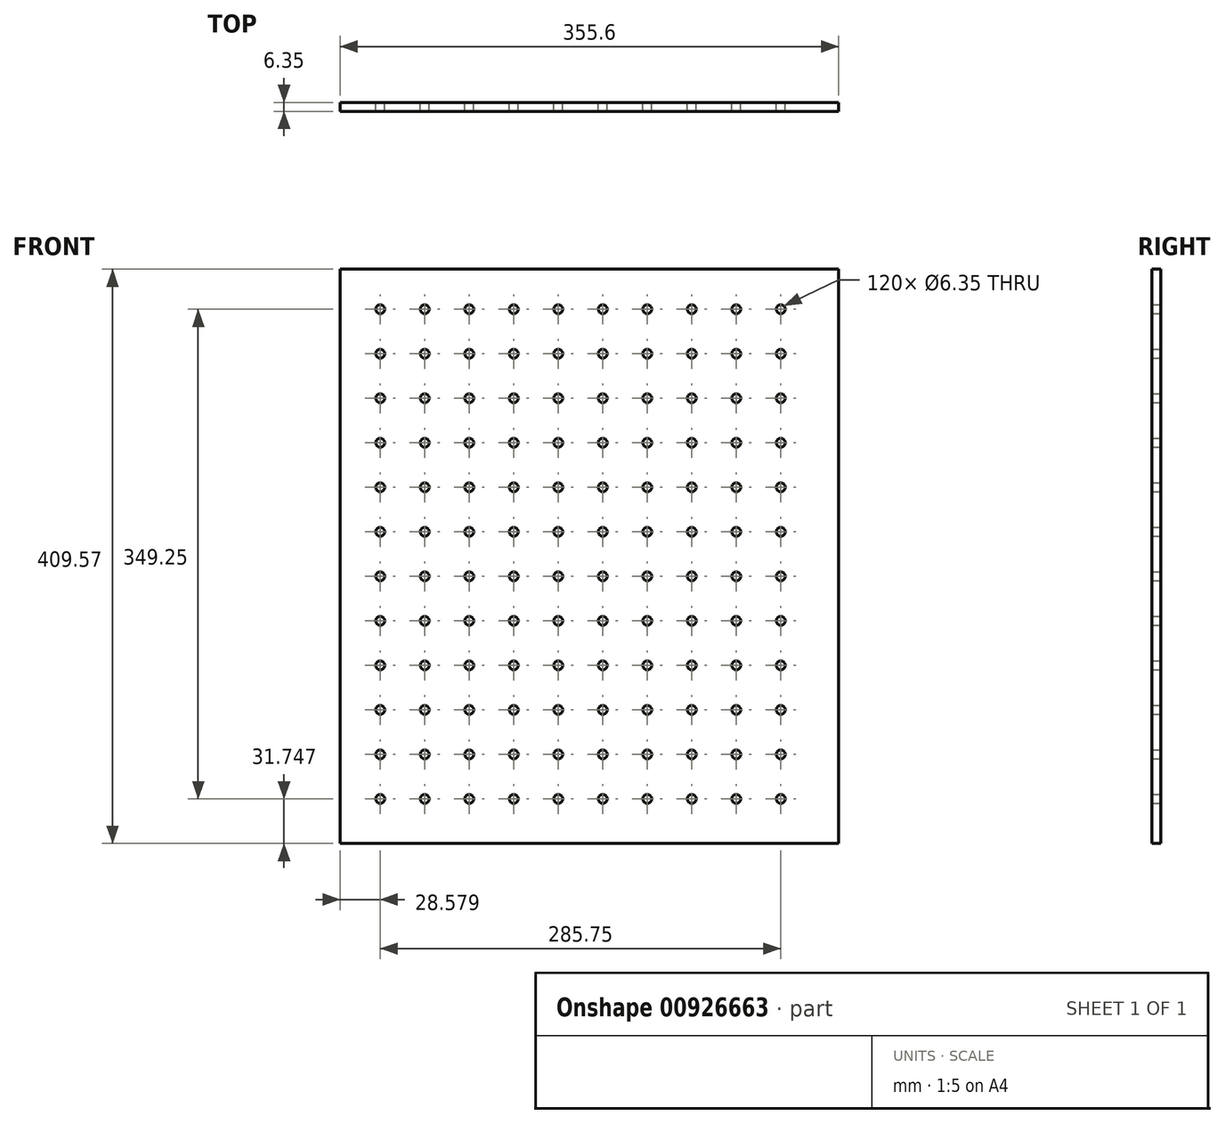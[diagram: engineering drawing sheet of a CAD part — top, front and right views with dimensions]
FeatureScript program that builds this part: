
annotation { "Feature Type Name" : "Feature", "Feature Type Description" : "" }
export const myFeature = defineFeature(function(context is Context, id is Id, definition is map)
    precondition{}
    {
        {
            var Q0;
            Q0=qCreatedBy(makeId("Front.planeOp"),FACE);
            var sketch = newSketch(context, id + "F0", { "sketchPlane" : qUnion([Q0])});
            skLineSegment(sketch, "E0.bottom", {"start": v(-178.08, 182.55) * mm, "end": v(177.52, 182.55) * mm});
            skLineSegment(sketch, "E0.top", {"start": v(-178.08, -227.02) * mm, "end": v(177.52, -227.02) * mm});
            skLineSegment(sketch, "E0.left", {"start": v(-178.08, 182.55) * mm, "end": v(-178.08, -227.02) * mm});
            skLineSegment(sketch, "E0.right", {"start": v(177.52, 182.55) * mm, "end": v(177.52, -227.02) * mm});
            skSolve(sketch);
        }
        {
            var Q0;
            Q0=makeQuery(id+"F0.imprint","IMPRINT",FACE,{"disambiguationData":[TD([[makeQuery(id+"F0.imprint","IMPRINT",EDGE,{"derivedFrom":sQuery(id+"F0.wireOp",EDGE,"E0.bottom")}),-1.0]])]});
            extrude(context, id + "F1", {"entities" : qUnion([Q0]), "depth" : 6.35 * mm, "offsetDistance" : 25.4 * mm});
        }
        {
            var Q0;
            Q0=makeQuery(id+"F1.opExtrude","CAP_FACE",FACE,{"disambiguationData":[OSD([sQuery(id+"F0.wireOp",EDGE,"E0.bottom"),sQuery(id+"F0.wireOp",EDGE,"E0.top"),sQuery(id+"F0.wireOp",EDGE,"E0.left"),sQuery(id+"F0.wireOp",EDGE,"E0.right")])],"isStart":false});
            var sketch = newSketch(context, id + "F2", { "sketchPlane" : qUnion([Q0])});
            skCircle(sketch, "E1", {"center": v(-149.5, 153.98) * mm, "radius": 3.18 * mm});
            skCircle(sketch, "E2", {"center": v(-117.75, 153.98) * mm, "radius": 3.18 * mm});
            skCircle(sketch, "E3", {"center": v(-86, 153.98) * mm, "radius": 3.18 * mm});
            skCircle(sketch, "E4", {"center": v(-54.25, 153.98) * mm, "radius": 3.18 * mm});
            skCircle(sketch, "E5", {"center": v(-22.5, 153.98) * mm, "radius": 3.18 * mm});
            skCircle(sketch, "E6", {"center": v(9.25, 153.98) * mm, "radius": 3.18 * mm});
            skCircle(sketch, "E7", {"center": v(41, 153.98) * mm, "radius": 3.18 * mm});
            skCircle(sketch, "E8", {"center": v(136.25, 153.98) * mm, "radius": 3.18 * mm});
            skCircle(sketch, "E9", {"center": v(104.5, 153.98) * mm, "radius": 3.18 * mm});
            skCircle(sketch, "E10", {"center": v(72.75, 153.98) * mm, "radius": 3.18 * mm});
            skSolve(sketch);
        }
        {
            var Q0;
            Q0=sQuery(id+"F2.wireOp",VERTEX,"E1.center");
            var Q1;
            Q1=sQuery(id+"F2.wireOp",VERTEX,"E2.center");
            var Q2;
            Q2=sQuery(id+"F2.wireOp",VERTEX,"E3.center");
            var Q3;
            Q3=sQuery(id+"F2.wireOp",VERTEX,"E4.center");
            var Q4;
            Q4=sQuery(id+"F2.wireOp",VERTEX,"E5.center");
            var Q5;
            Q5=sQuery(id+"F2.wireOp",VERTEX,"E6.center");
            var Q6;
            Q6=sQuery(id+"F2.wireOp",VERTEX,"E7.center");
            var Q7;
            Q7=sQuery(id+"F2.wireOp",VERTEX,"E10.center");
            var Q8;
            Q8=sQuery(id+"F2.wireOp",VERTEX,"E9.center");
            var Q9;
            Q9=sQuery(id+"F2.wireOp",VERTEX,"E8.center");
            var Q10;
            Q10=makeQuery(id+"F1.opExtrude","SWEPT_BODY",BODY,{"disambiguationData":[OSD([sQuery(id+"F0.wireOp",EDGE,"E0.bottom"),sQuery(id+"F0.wireOp",EDGE,"E0.top"),sQuery(id+"F0.wireOp",EDGE,"E0.left"),sQuery(id+"F0.wireOp",EDGE,"E0.right")])]});
            hole(context, id + "F3", {"style" : HoleStyle.SIMPLE, "endStyle" : HoleEndStyle.THROUGH, "holeDiameter" : 6.35 * mm, "majorDiameter" : 6.35 * mm, "isTappedThrough" : true, "tappedDepth" : 12.7 * mm, "tapClearance" : 3, "locations" : qUnion([Q0, Q1, Q2, Q3, Q4, Q5, Q6, Q7, Q8, Q9]), "scope" : qUnion([Q10])});
        }
        {
            var Q0;
            Q0=makeQuery(id+"F1.opExtrude","CAP_FACE",FACE,{"disambiguationData":[OSD([sQuery(id+"F0.wireOp",EDGE,"E0.bottom"),sQuery(id+"F0.wireOp",EDGE,"E0.top"),sQuery(id+"F0.wireOp",EDGE,"E0.left"),sQuery(id+"F0.wireOp",EDGE,"E0.right")])],"isStart":false});
            var sketch = newSketch(context, id + "F4", { "sketchPlane" : qUnion([Q0])});
            skCircle(sketch, "E11", {"center": v(-149.5, 122.23) * mm, "radius": 3.18 * mm});
            skCircle(sketch, "E12", {"center": v(-117.75, 122.23) * mm, "radius": 3.18 * mm});
            skCircle(sketch, "E13", {"center": v(-86, 122.23) * mm, "radius": 3.18 * mm});
            skCircle(sketch, "E14", {"center": v(-54.25, 122.23) * mm, "radius": 3.18 * mm});
            skCircle(sketch, "E15", {"center": v(-22.5, 122.23) * mm, "radius": 3.18 * mm});
            skCircle(sketch, "E16", {"center": v(9.25, 122.23) * mm, "radius": 3.18 * mm});
            skCircle(sketch, "E17", {"center": v(41, 122.23) * mm, "radius": 3.18 * mm});
            skCircle(sketch, "E18", {"center": v(136.25, 122.23) * mm, "radius": 3.18 * mm});
            skCircle(sketch, "E19", {"center": v(104.5, 122.23) * mm, "radius": 3.18 * mm});
            skCircle(sketch, "E20", {"center": v(72.75, 122.23) * mm, "radius": 3.18 * mm});
            skSolve(sketch);
        }
        {
            var Q0;
            Q0=sQuery(id+"F4.wireOp",VERTEX,"E11.center");
            var Q1;
            Q1=sQuery(id+"F4.wireOp",VERTEX,"E12.center");
            var Q2;
            Q2=sQuery(id+"F4.wireOp",VERTEX,"E13.center");
            var Q3;
            Q3=sQuery(id+"F4.wireOp",VERTEX,"E14.center");
            var Q4;
            Q4=sQuery(id+"F4.wireOp",VERTEX,"E15.center");
            var Q5;
            Q5=sQuery(id+"F4.wireOp",VERTEX,"E16.center");
            var Q6;
            Q6=sQuery(id+"F4.wireOp",VERTEX,"E17.center");
            var Q7;
            Q7=sQuery(id+"F4.wireOp",VERTEX,"E20.center");
            var Q8;
            Q8=sQuery(id+"F4.wireOp",VERTEX,"E19.center");
            var Q9;
            Q9=sQuery(id+"F4.wireOp",VERTEX,"E18.center");
            var Q10;
            Q10=makeQuery(id+"F1.opExtrude","SWEPT_BODY",BODY,{"disambiguationData":[OSD([sQuery(id+"F0.wireOp",EDGE,"E0.bottom"),sQuery(id+"F0.wireOp",EDGE,"E0.top"),sQuery(id+"F0.wireOp",EDGE,"E0.left"),sQuery(id+"F0.wireOp",EDGE,"E0.right")])]});
            hole(context, id + "F5", {"style" : HoleStyle.SIMPLE, "endStyle" : HoleEndStyle.THROUGH, "holeDiameter" : 6.35 * mm, "majorDiameter" : 6.35 * mm, "isTappedThrough" : true, "tappedDepth" : 12.7 * mm, "tapClearance" : 3, "locations" : qUnion([Q0, Q1, Q2, Q3, Q4, Q5, Q6, Q7, Q8, Q9]), "scope" : qUnion([Q10])});
        }
        {
            var Q0;
            Q0=makeQuery(id+"F1.opExtrude","CAP_FACE",FACE,{"disambiguationData":[OSD([sQuery(id+"F0.wireOp",EDGE,"E0.bottom"),sQuery(id+"F0.wireOp",EDGE,"E0.top"),sQuery(id+"F0.wireOp",EDGE,"E0.left"),sQuery(id+"F0.wireOp",EDGE,"E0.right")])],"isStart":false});
            var sketch = newSketch(context, id + "F6", { "sketchPlane" : qUnion([Q0])});
            skCircle(sketch, "E21", {"center": v(-149.5, 90.48) * mm, "radius": 3.18 * mm});
            skCircle(sketch, "E22", {"center": v(-117.75, 90.48) * mm, "radius": 3.18 * mm});
            skCircle(sketch, "E23", {"center": v(-86, 90.48) * mm, "radius": 3.18 * mm});
            skCircle(sketch, "E24", {"center": v(-54.25, 90.48) * mm, "radius": 3.18 * mm});
            skCircle(sketch, "E25", {"center": v(-22.5, 90.48) * mm, "radius": 3.18 * mm});
            skCircle(sketch, "E26", {"center": v(9.25, 90.48) * mm, "radius": 3.18 * mm});
            skCircle(sketch, "E27", {"center": v(41, 90.48) * mm, "radius": 3.18 * mm});
            skCircle(sketch, "E28", {"center": v(136.25, 90.48) * mm, "radius": 3.18 * mm});
            skCircle(sketch, "E29", {"center": v(104.5, 90.48) * mm, "radius": 3.18 * mm});
            skCircle(sketch, "E30", {"center": v(72.75, 90.48) * mm, "radius": 3.18 * mm});
            skCircle(sketch, "E31", {"center": v(-149.5, 58.73) * mm, "radius": 3.18 * mm});
            skCircle(sketch, "E32", {"center": v(-117.75, 58.73) * mm, "radius": 3.18 * mm});
            skCircle(sketch, "E33", {"center": v(-86, 58.73) * mm, "radius": 3.18 * mm});
            skCircle(sketch, "E34", {"center": v(-54.25, 58.73) * mm, "radius": 3.18 * mm});
            skCircle(sketch, "E35", {"center": v(-22.5, 58.73) * mm, "radius": 3.18 * mm});
            skCircle(sketch, "E36", {"center": v(9.25, 58.73) * mm, "radius": 3.18 * mm});
            skCircle(sketch, "E37", {"center": v(41, 58.73) * mm, "radius": 3.18 * mm});
            skCircle(sketch, "E38", {"center": v(136.25, 58.73) * mm, "radius": 3.18 * mm});
            skCircle(sketch, "E39", {"center": v(104.5, 58.73) * mm, "radius": 3.18 * mm});
            skCircle(sketch, "E40", {"center": v(72.75, 58.73) * mm, "radius": 3.18 * mm});
            skCircle(sketch, "E41", {"center": v(-149.5, 26.98) * mm, "radius": 3.18 * mm});
            skCircle(sketch, "E42", {"center": v(-117.75, 26.98) * mm, "radius": 3.18 * mm});
            skCircle(sketch, "E43", {"center": v(-86, 26.98) * mm, "radius": 3.18 * mm});
            skCircle(sketch, "E44", {"center": v(-54.25, 26.98) * mm, "radius": 3.18 * mm});
            skCircle(sketch, "E45", {"center": v(-22.5, 26.98) * mm, "radius": 3.18 * mm});
            skCircle(sketch, "E46", {"center": v(9.25, 26.98) * mm, "radius": 3.18 * mm});
            skCircle(sketch, "E47", {"center": v(41, 26.98) * mm, "radius": 3.18 * mm});
            skCircle(sketch, "E48", {"center": v(136.25, 26.98) * mm, "radius": 3.18 * mm});
            skCircle(sketch, "E49", {"center": v(104.5, 26.98) * mm, "radius": 3.18 * mm});
            skCircle(sketch, "E50", {"center": v(72.75, 26.98) * mm, "radius": 3.18 * mm});
            skCircle(sketch, "E51", {"center": v(-149.5, -4.77) * mm, "radius": 3.18 * mm});
            skCircle(sketch, "E52", {"center": v(-117.75, -4.77) * mm, "radius": 3.18 * mm});
            skCircle(sketch, "E53", {"center": v(-86, -4.77) * mm, "radius": 3.18 * mm});
            skCircle(sketch, "E54", {"center": v(-54.25, -4.77) * mm, "radius": 3.18 * mm});
            skCircle(sketch, "E55", {"center": v(-22.5, -4.77) * mm, "radius": 3.18 * mm});
            skCircle(sketch, "E56", {"center": v(9.25, -4.77) * mm, "radius": 3.18 * mm});
            skCircle(sketch, "E57", {"center": v(41, -4.77) * mm, "radius": 3.18 * mm});
            skCircle(sketch, "E58", {"center": v(136.25, -4.77) * mm, "radius": 3.18 * mm});
            skCircle(sketch, "E59", {"center": v(104.5, -4.77) * mm, "radius": 3.18 * mm});
            skCircle(sketch, "E60", {"center": v(72.75, -4.77) * mm, "radius": 3.18 * mm});
            skCircle(sketch, "E61", {"center": v(-149.5, -36.52) * mm, "radius": 3.18 * mm});
            skCircle(sketch, "E62", {"center": v(-117.75, -36.52) * mm, "radius": 3.18 * mm});
            skCircle(sketch, "E63", {"center": v(-86, -36.52) * mm, "radius": 3.18 * mm});
            skCircle(sketch, "E64", {"center": v(-54.25, -36.52) * mm, "radius": 3.18 * mm});
            skCircle(sketch, "E65", {"center": v(-22.5, -36.52) * mm, "radius": 3.18 * mm});
            skCircle(sketch, "E66", {"center": v(9.25, -36.52) * mm, "radius": 3.18 * mm});
            skCircle(sketch, "E67", {"center": v(41, -36.52) * mm, "radius": 3.18 * mm});
            skCircle(sketch, "E68", {"center": v(136.25, -36.52) * mm, "radius": 3.18 * mm});
            skCircle(sketch, "E69", {"center": v(104.5, -36.52) * mm, "radius": 3.18 * mm});
            skCircle(sketch, "E70", {"center": v(72.75, -36.52) * mm, "radius": 3.18 * mm});
            skCircle(sketch, "E71", {"center": v(-149.5, -68.27) * mm, "radius": 3.18 * mm});
            skCircle(sketch, "E72", {"center": v(-117.75, -68.27) * mm, "radius": 3.18 * mm});
            skCircle(sketch, "E73", {"center": v(-86, -68.27) * mm, "radius": 3.18 * mm});
            skCircle(sketch, "E74", {"center": v(-54.25, -68.27) * mm, "radius": 3.18 * mm});
            skCircle(sketch, "E75", {"center": v(-22.5, -68.27) * mm, "radius": 3.18 * mm});
            skCircle(sketch, "E76", {"center": v(9.25, -68.27) * mm, "radius": 3.18 * mm});
            skCircle(sketch, "E77", {"center": v(41, -68.27) * mm, "radius": 3.18 * mm});
            skCircle(sketch, "E78", {"center": v(136.25, -68.27) * mm, "radius": 3.18 * mm});
            skCircle(sketch, "E79", {"center": v(104.5, -68.27) * mm, "radius": 3.18 * mm});
            skCircle(sketch, "E80", {"center": v(72.75, -68.27) * mm, "radius": 3.18 * mm});
            skCircle(sketch, "E81", {"center": v(-149.5, -100.02) * mm, "radius": 3.18 * mm});
            skCircle(sketch, "E82", {"center": v(-117.75, -100.02) * mm, "radius": 3.18 * mm});
            skCircle(sketch, "E83", {"center": v(-86, -100.02) * mm, "radius": 3.18 * mm});
            skCircle(sketch, "E84", {"center": v(-54.25, -100.02) * mm, "radius": 3.18 * mm});
            skCircle(sketch, "E85", {"center": v(-22.5, -100.02) * mm, "radius": 3.18 * mm});
            skCircle(sketch, "E86", {"center": v(9.25, -100.02) * mm, "radius": 3.18 * mm});
            skCircle(sketch, "E87", {"center": v(41, -100.02) * mm, "radius": 3.18 * mm});
            skCircle(sketch, "E88", {"center": v(136.25, -100.02) * mm, "radius": 3.18 * mm});
            skCircle(sketch, "E89", {"center": v(104.5, -100.02) * mm, "radius": 3.18 * mm});
            skCircle(sketch, "E90", {"center": v(72.75, -100.02) * mm, "radius": 3.18 * mm});
            skCircle(sketch, "E91", {"center": v(-149.5, -131.77) * mm, "radius": 3.18 * mm});
            skCircle(sketch, "E92", {"center": v(-117.75, -131.77) * mm, "radius": 3.18 * mm});
            skCircle(sketch, "E93", {"center": v(-86, -131.77) * mm, "radius": 3.18 * mm});
            skCircle(sketch, "E94", {"center": v(-54.25, -131.77) * mm, "radius": 3.18 * mm});
            skCircle(sketch, "E95", {"center": v(-22.5, -131.77) * mm, "radius": 3.18 * mm});
            skCircle(sketch, "E96", {"center": v(9.25, -131.77) * mm, "radius": 3.18 * mm});
            skCircle(sketch, "E97", {"center": v(41, -131.77) * mm, "radius": 3.18 * mm});
            skCircle(sketch, "E98", {"center": v(136.25, -131.77) * mm, "radius": 3.18 * mm});
            skCircle(sketch, "E99", {"center": v(104.5, -131.77) * mm, "radius": 3.18 * mm});
            skCircle(sketch, "E100", {"center": v(72.75, -131.77) * mm, "radius": 3.18 * mm});
            skCircle(sketch, "E101", {"center": v(-149.5, -163.52) * mm, "radius": 3.18 * mm});
            skCircle(sketch, "E102", {"center": v(-117.75, -163.52) * mm, "radius": 3.18 * mm});
            skCircle(sketch, "E103", {"center": v(-86, -163.52) * mm, "radius": 3.18 * mm});
            skCircle(sketch, "E104", {"center": v(-54.25, -163.52) * mm, "radius": 3.18 * mm});
            skCircle(sketch, "E105", {"center": v(-22.5, -163.52) * mm, "radius": 3.18 * mm});
            skCircle(sketch, "E106", {"center": v(9.25, -163.52) * mm, "radius": 3.18 * mm});
            skCircle(sketch, "E107", {"center": v(41, -163.52) * mm, "radius": 3.18 * mm});
            skCircle(sketch, "E108", {"center": v(136.25, -163.52) * mm, "radius": 3.18 * mm});
            skCircle(sketch, "E109", {"center": v(104.5, -163.52) * mm, "radius": 3.18 * mm});
            skCircle(sketch, "E110", {"center": v(72.75, -163.52) * mm, "radius": 3.18 * mm});
            skCircle(sketch, "E111", {"center": v(-149.5, -195.27) * mm, "radius": 3.18 * mm});
            skCircle(sketch, "E112", {"center": v(-117.75, -195.27) * mm, "radius": 3.18 * mm});
            skCircle(sketch, "E113", {"center": v(-86, -195.27) * mm, "radius": 3.18 * mm});
            skCircle(sketch, "E114", {"center": v(-54.25, -195.27) * mm, "radius": 3.18 * mm});
            skCircle(sketch, "E115", {"center": v(-22.5, -195.27) * mm, "radius": 3.18 * mm});
            skCircle(sketch, "E116", {"center": v(9.25, -195.27) * mm, "radius": 3.18 * mm});
            skCircle(sketch, "E117", {"center": v(41, -195.27) * mm, "radius": 3.18 * mm});
            skCircle(sketch, "E118", {"center": v(136.25, -195.27) * mm, "radius": 3.18 * mm});
            skCircle(sketch, "E119", {"center": v(104.5, -195.27) * mm, "radius": 3.18 * mm});
            skCircle(sketch, "E120", {"center": v(72.75, -195.27) * mm, "radius": 3.18 * mm});
            skSolve(sketch);
        }
        {
            var Q0;
            Q0=sQuery(id+"F6.wireOp",VERTEX,"E60.center");
            var Q1;
            Q1=sQuery(id+"F6.wireOp",VERTEX,"E71.center");
            var Q2;
            Q2=sQuery(id+"F6.wireOp",VERTEX,"E30.center");
            var Q3;
            Q3=sQuery(id+"F6.wireOp",VERTEX,"E26.center");
            var Q4;
            Q4=sQuery(id+"F6.wireOp",VERTEX,"E105.center");
            var Q5;
            Q5=sQuery(id+"F6.wireOp",VERTEX,"E96.center");
            var Q6;
            Q6=sQuery(id+"F6.wireOp",VERTEX,"E31.center");
            var Q7;
            Q7=sQuery(id+"F6.wireOp",VERTEX,"E38.center");
            var Q8;
            Q8=sQuery(id+"F6.wireOp",VERTEX,"E98.center");
            var Q9;
            Q9=sQuery(id+"F6.wireOp",VERTEX,"E77.center");
            var Q10;
            Q10=sQuery(id+"F6.wireOp",VERTEX,"E101.center");
            var Q11;
            Q11=sQuery(id+"F6.wireOp",VERTEX,"E34.center");
            var Q12;
            Q12=sQuery(id+"F6.wireOp",VERTEX,"E52.center");
            var Q13;
            Q13=sQuery(id+"F6.wireOp",VERTEX,"E118.center");
            var Q14;
            Q14=sQuery(id+"F6.wireOp",VERTEX,"E115.center");
            var Q15;
            Q15=sQuery(id+"F6.wireOp",VERTEX,"E48.center");
            var Q16;
            Q16=sQuery(id+"F6.wireOp",VERTEX,"E111.center");
            var Q17;
            Q17=sQuery(id+"F6.wireOp",VERTEX,"E35.center");
            var Q18;
            Q18=sQuery(id+"F6.wireOp",VERTEX,"E44.center");
            var Q19;
            Q19=sQuery(id+"F6.wireOp",VERTEX,"E28.center");
            var Q20;
            Q20=sQuery(id+"F6.wireOp",VERTEX,"E21.center");
            var Q21;
            Q21=sQuery(id+"F6.wireOp",VERTEX,"E104.center");
            var Q22;
            Q22=sQuery(id+"F6.wireOp",VERTEX,"E86.center");
            var Q23;
            Q23=sQuery(id+"F6.wireOp",VERTEX,"E23.center");
            var Q24;
            Q24=sQuery(id+"F6.wireOp",VERTEX,"E64.center");
            var Q25;
            Q25=sQuery(id+"F6.wireOp",VERTEX,"E55.center");
            var Q26;
            Q26=sQuery(id+"F6.wireOp",VERTEX,"E87.center");
            var Q27;
            Q27=sQuery(id+"F6.wireOp",VERTEX,"E47.center");
            var Q28;
            Q28=sQuery(id+"F6.wireOp",VERTEX,"E84.center");
            var Q29;
            Q29=sQuery(id+"F6.wireOp",VERTEX,"E114.center");
            var Q30;
            Q30=sQuery(id+"F6.wireOp",VERTEX,"E72.center");
            var Q31;
            Q31=sQuery(id+"F6.wireOp",VERTEX,"E109.center");
            var Q32;
            Q32=sQuery(id+"F6.wireOp",VERTEX,"E65.center");
            var Q33;
            Q33=sQuery(id+"F6.wireOp",VERTEX,"E93.center");
            var Q34;
            Q34=sQuery(id+"F6.wireOp",VERTEX,"E116.center");
            var Q35;
            Q35=sQuery(id+"F6.wireOp",VERTEX,"E56.center");
            var Q36;
            Q36=sQuery(id+"F6.wireOp",VERTEX,"E81.center");
            var Q37;
            Q37=sQuery(id+"F6.wireOp",VERTEX,"E120.center");
            var Q38;
            Q38=sQuery(id+"F6.wireOp",VERTEX,"E27.center");
            var Q39;
            Q39=sQuery(id+"F6.wireOp",VERTEX,"E78.center");
            var Q40;
            Q40=sQuery(id+"F6.wireOp",VERTEX,"E50.center");
            var Q41;
            Q41=sQuery(id+"F6.wireOp",VERTEX,"E67.center");
            var Q42;
            Q42=sQuery(id+"F6.wireOp",VERTEX,"E110.center");
            var Q43;
            Q43=sQuery(id+"F6.wireOp",VERTEX,"E94.center");
            var Q44;
            Q44=sQuery(id+"F6.wireOp",VERTEX,"E88.center");
            var Q45;
            Q45=sQuery(id+"F6.wireOp",VERTEX,"E90.center");
            var Q46;
            Q46=sQuery(id+"F6.wireOp",VERTEX,"E74.center");
            var Q47;
            Q47=sQuery(id+"F6.wireOp",VERTEX,"E75.center");
            var Q48;
            Q48=sQuery(id+"F6.wireOp",VERTEX,"E73.center");
            var Q49;
            Q49=sQuery(id+"F6.wireOp",VERTEX,"E49.center");
            var Q50;
            Q50=sQuery(id+"F6.wireOp",VERTEX,"E63.center");
            var Q51;
            Q51=sQuery(id+"F6.wireOp",VERTEX,"E53.center");
            var Q52;
            Q52=sQuery(id+"F6.wireOp",VERTEX,"E51.center");
            var Q53;
            Q53=sQuery(id+"F6.wireOp",VERTEX,"E58.center");
            var Q54;
            Q54=sQuery(id+"F6.wireOp",VERTEX,"E66.center");
            var Q55;
            Q55=sQuery(id+"F6.wireOp",VERTEX,"E68.center");
            var Q56;
            Q56=sQuery(id+"F6.wireOp",VERTEX,"E91.center");
            var Q57;
            Q57=sQuery(id+"F6.wireOp",VERTEX,"E106.center");
            var Q58;
            Q58=sQuery(id+"F6.wireOp",VERTEX,"E54.center");
            var Q59;
            Q59=sQuery(id+"F6.wireOp",VERTEX,"E102.center");
            var Q60;
            Q60=sQuery(id+"F6.wireOp",VERTEX,"E57.center");
            var Q61;
            Q61=sQuery(id+"F6.wireOp",VERTEX,"E25.center");
            var Q62;
            Q62=sQuery(id+"F6.wireOp",VERTEX,"E117.center");
            var Q63;
            Q63=sQuery(id+"F6.wireOp",VERTEX,"E113.center");
            var Q64;
            Q64=sQuery(id+"F6.wireOp",VERTEX,"E59.center");
            var Q65;
            Q65=sQuery(id+"F6.wireOp",VERTEX,"E103.center");
            var Q66;
            Q66=sQuery(id+"F6.wireOp",VERTEX,"E61.center");
            var Q67;
            Q67=sQuery(id+"F6.wireOp",VERTEX,"E22.center");
            var Q68;
            Q68=sQuery(id+"F6.wireOp",VERTEX,"E42.center");
            var Q69;
            Q69=sQuery(id+"F6.wireOp",VERTEX,"E97.center");
            var Q70;
            Q70=sQuery(id+"F6.wireOp",VERTEX,"E24.center");
            var Q71;
            Q71=sQuery(id+"F6.wireOp",VERTEX,"E43.center");
            var Q72;
            Q72=sQuery(id+"F6.wireOp",VERTEX,"E112.center");
            var Q73;
            Q73=sQuery(id+"F6.wireOp",VERTEX,"E29.center");
            var Q74;
            Q74=sQuery(id+"F6.wireOp",VERTEX,"E83.center");
            var Q75;
            Q75=sQuery(id+"F6.wireOp",VERTEX,"E36.center");
            var Q76;
            Q76=sQuery(id+"F6.wireOp",VERTEX,"E45.center");
            var Q77;
            Q77=sQuery(id+"F6.wireOp",VERTEX,"E119.center");
            var Q78;
            Q78=sQuery(id+"F6.wireOp",VERTEX,"E40.center");
            var Q79;
            Q79=sQuery(id+"F6.wireOp",VERTEX,"E82.center");
            var Q80;
            Q80=sQuery(id+"F6.wireOp",VERTEX,"E76.center");
            var Q81;
            Q81=sQuery(id+"F6.wireOp",VERTEX,"E70.center");
            var Q82;
            Q82=sQuery(id+"F6.wireOp",VERTEX,"E33.center");
            var Q83;
            Q83=sQuery(id+"F6.wireOp",VERTEX,"E39.center");
            var Q84;
            Q84=sQuery(id+"F6.wireOp",VERTEX,"E37.center");
            var Q85;
            Q85=sQuery(id+"F6.wireOp",VERTEX,"E89.center");
            var Q86;
            Q86=sQuery(id+"F6.wireOp",VERTEX,"E108.center");
            var Q87;
            Q87=sQuery(id+"F6.wireOp",VERTEX,"E99.center");
            var Q88;
            Q88=sQuery(id+"F6.wireOp",VERTEX,"E80.center");
            var Q89;
            Q89=sQuery(id+"F6.wireOp",VERTEX,"E32.center");
            var Q90;
            Q90=sQuery(id+"F6.wireOp",VERTEX,"E95.center");
            var Q91;
            Q91=sQuery(id+"F6.wireOp",VERTEX,"E100.center");
            var Q92;
            Q92=sQuery(id+"F6.wireOp",VERTEX,"E107.center");
            var Q93;
            Q93=sQuery(id+"F6.wireOp",VERTEX,"E79.center");
            var Q94;
            Q94=sQuery(id+"F6.wireOp",VERTEX,"E41.center");
            var Q95;
            Q95=sQuery(id+"F6.wireOp",VERTEX,"E92.center");
            var Q96;
            Q96=sQuery(id+"F6.wireOp",VERTEX,"E85.center");
            var Q97;
            Q97=sQuery(id+"F6.wireOp",VERTEX,"E62.center");
            var Q98;
            Q98=sQuery(id+"F6.wireOp",VERTEX,"E69.center");
            var Q99;
            Q99=sQuery(id+"F6.wireOp",VERTEX,"E46.center");
            var Q100;
            Q100=makeQuery(id+"F1.opExtrude","SWEPT_BODY",BODY,{"disambiguationData":[OSD([sQuery(id+"F0.wireOp",EDGE,"E0.bottom"),sQuery(id+"F0.wireOp",EDGE,"E0.top"),sQuery(id+"F0.wireOp",EDGE,"E0.left"),sQuery(id+"F0.wireOp",EDGE,"E0.right")])]});
            hole(context, id + "F7", {"style" : HoleStyle.SIMPLE, "endStyle" : HoleEndStyle.THROUGH, "holeDiameter" : 6.35 * mm, "majorDiameter" : 6.35 * mm, "isTappedThrough" : true, "tappedDepth" : 12.7 * mm, "tapClearance" : 3, "locations" : qUnion([Q0, Q1, Q2, Q3, Q4, Q5, Q6, Q7, Q8, Q9, Q10, Q11, Q12, Q13, Q14, Q15, Q16, Q17, Q18, Q19, Q20, Q21, Q22, Q23, Q24, Q25, Q26, Q27, Q28, Q29, Q30, Q31, Q32, Q33, Q34, Q35, Q36, Q37, Q38, Q39, Q40, Q41, Q42, Q43, Q44, Q45, Q46, Q47, Q48, Q49, Q50, Q51, Q52, Q53, Q54, Q55, Q56, Q57, Q58, Q59, Q60, Q61, Q62, Q63, Q64, Q65, Q66, Q67, Q68, Q69, Q70, Q71, Q72, Q73, Q74, Q75, Q76, Q77, Q78, Q79, Q80, Q81, Q82, Q83, Q84, Q85, Q86, Q87, Q88, Q89, Q90, Q91, Q92, Q93, Q94, Q95, Q96, Q97, Q98, Q99]), "scope" : qUnion([Q100])});
        }
    });
